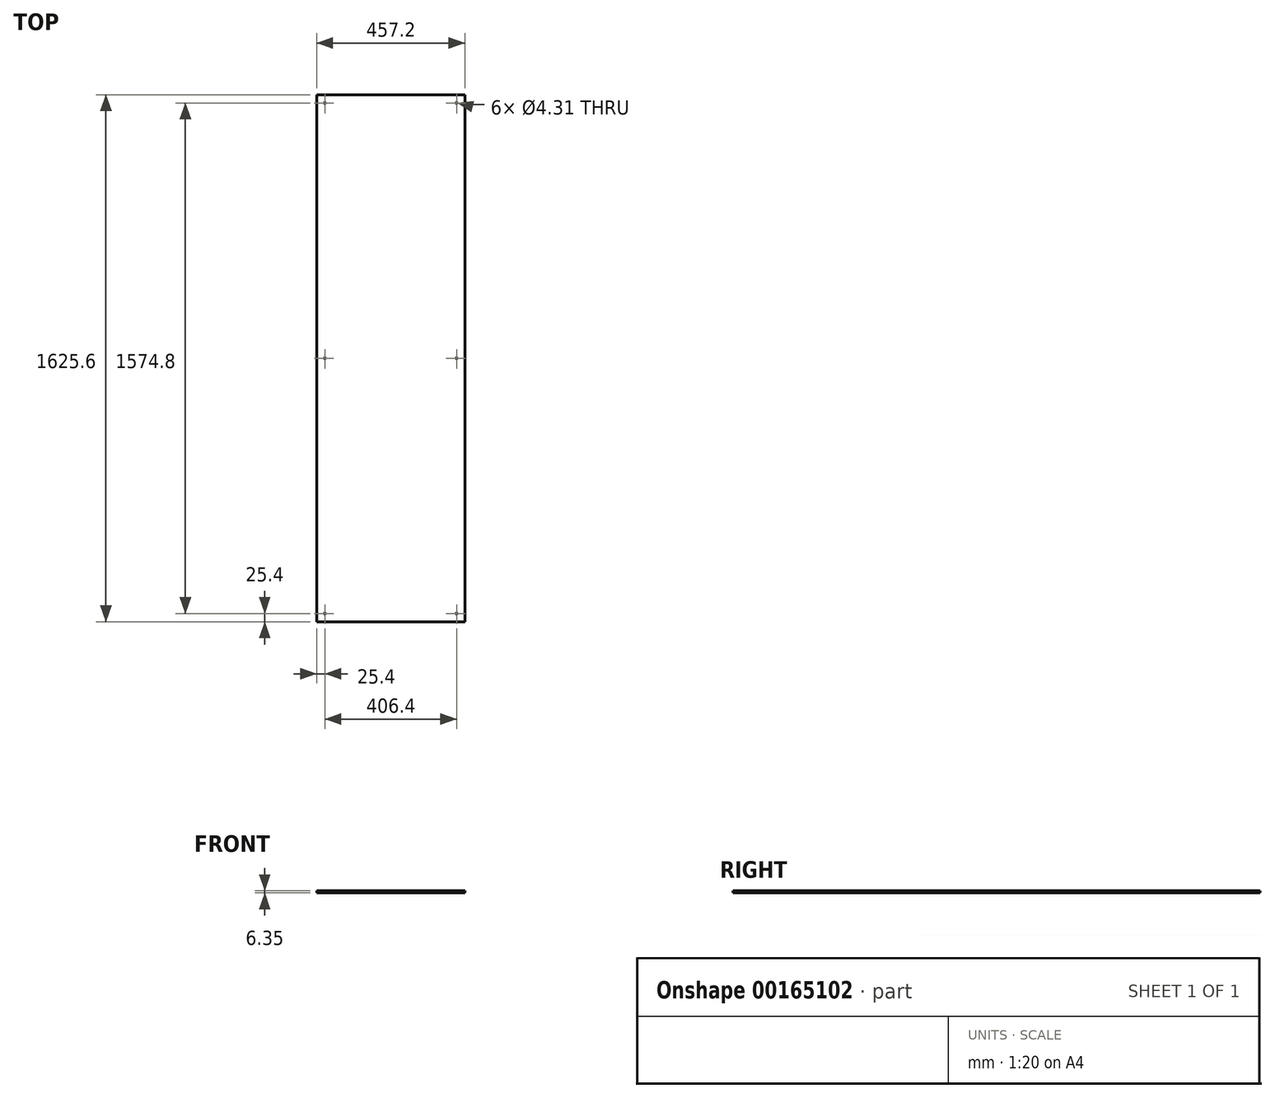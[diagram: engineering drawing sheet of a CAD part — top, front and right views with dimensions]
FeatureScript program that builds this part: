
annotation { "Feature Type Name" : "Feature", "Feature Type Description" : "" }
export const myFeature = defineFeature(function(context is Context, id is Id, definition is map)
    precondition{}
    {
        {
            var Q0;
            Q0=qCreatedBy(makeId("Top.planeOp"),FACE);
            var sketch = newSketch(context, id + "F0", { "sketchPlane" : qUnion([Q0])});
            skPoint(sketch, "E0.middle", {"position": v(0, 0) * mm});
            skLineSegment(sketch, "E1.bottom", {"start": v(228.6, -812.8) * mm, "end": v(-228.6, -812.8) * mm});
            skLineSegment(sketch, "E1.top", {"start": v(228.6, 812.8) * mm, "end": v(-228.6, 812.8) * mm});
            skLineSegment(sketch, "E1.left", {"start": v(228.6, -812.8) * mm, "end": v(228.6, 812.8) * mm});
            skLineSegment(sketch, "E1.right", {"start": v(-228.6, -812.8) * mm, "end": v(-228.6, 812.8) * mm});
            skSolve(sketch);
        }
        {
            var Q0;
            Q0=qSketchRegion(id+"F0",true);
            extrude(context, id + "F1", {"entities" : qUnion([Q0]), "depth" : 6.35 * mm});
        }
        {
            var Q0;
            Q0=makeQuery(id+"F1.opExtrude","CAP_FACE",FACE,{"disambiguationData":[OSD([sQuery(id+"F0.wireOp",EDGE,"E0.bottom"),sQuery(id+"F0.wireOp",EDGE,"E0.top"),sQuery(id+"F0.wireOp",EDGE,"E0.left"),sQuery(id+"F0.wireOp",EDGE,"E0.right"),sQuery(id+"F0.wireOp",EDGE,"E1.bottom"),sQuery(id+"F0.wireOp",EDGE,"E1.top"),sQuery(id+"F0.wireOp",EDGE,"E1.left"),sQuery(id+"F0.wireOp",EDGE,"E1.right")])],"isStart":false});
            var sketch = newSketch(context, id + "F2", { "sketchPlane" : qUnion([Q0])});
            skLineSegment(sketch, "E2.bottom", {"start": v(-203.2, -787.4) * mm, "end": v(203.2, -787.4) * mm, "construction": true});
            skLineSegment(sketch, "E2.top", {"start": v(-203.2, 787.4) * mm, "end": v(203.2, 787.4) * mm, "construction": true});
            skLineSegment(sketch, "E2.left", {"start": v(-203.2, -787.4) * mm, "end": v(-203.2, 787.4) * mm, "construction": true});
            skLineSegment(sketch, "E2.right", {"start": v(203.2, -787.4) * mm, "end": v(203.2, 787.4) * mm, "construction": true});
            skPoint(sketch, "E2.middle", {"position": v(0, 0) * mm});
            skLineSegment(sketch, "E3.bottom", {"start": v(-203.2, -787.4) * mm, "end": v(-228.6, -787.4) * mm, "construction": true});
            skLineSegment(sketch, "E3.top", {"start": v(-203.2, -812.8) * mm, "end": v(-228.6, -812.8) * mm, "construction": true});
            skLineSegment(sketch, "E3.left", {"start": v(-203.2, -787.4) * mm, "end": v(-203.2, -812.8) * mm, "construction": true});
            skLineSegment(sketch, "E3.right", {"start": v(-228.6, -787.4) * mm, "end": v(-228.6, -812.8) * mm, "construction": true});
            skCircle(sketch, "E4", {"center": v(-203.2, -787.4) * mm, "radius": 2.15 * mm});
            skCircle(sketch, "E5", {"center": v(203.2, -787.4) * mm, "radius": 2.15 * mm});
            skCircle(sketch, "E6", {"center": v(203.2, 0) * mm, "radius": 2.15 * mm});
            skCircle(sketch, "E7", {"center": v(-203.2, 0) * mm, "radius": 2.15 * mm});
            skCircle(sketch, "E8", {"center": v(-203.2, 787.4) * mm, "radius": 2.15 * mm});
            skCircle(sketch, "E9", {"center": v(203.2, 787.4) * mm, "radius": 2.15 * mm});
            skSolve(sketch);
        }
        {
            var Q0;
            Q0=qSketchRegion(id+"F2",true);
            var Q1;
            Q1=makeQuery(id+"F1.opExtrude","CAP_FACE",FACE,{"disambiguationData":[OSD([sQuery(id+"F0.wireOp",EDGE,"E0.bottom"),sQuery(id+"F0.wireOp",EDGE,"E0.top"),sQuery(id+"F0.wireOp",EDGE,"E0.left"),sQuery(id+"F0.wireOp",EDGE,"E0.right"),sQuery(id+"F0.wireOp",EDGE,"E1.bottom"),sQuery(id+"F0.wireOp",EDGE,"E1.top"),sQuery(id+"F0.wireOp",EDGE,"E1.left"),sQuery(id+"F0.wireOp",EDGE,"E1.right")])],"isStart":true});
            extrude(context, id + "F3", {"entities" : qUnion([Q0]), "operationType" : NewBodyOperationType.REMOVE, "endBound" : BoundingType.UP_TO_SURFACE, "oppositeDirection" : true, "endBoundEntityFace" : qUnion([Q1]), "depth" : 25.4 * mm});
        }
    });
